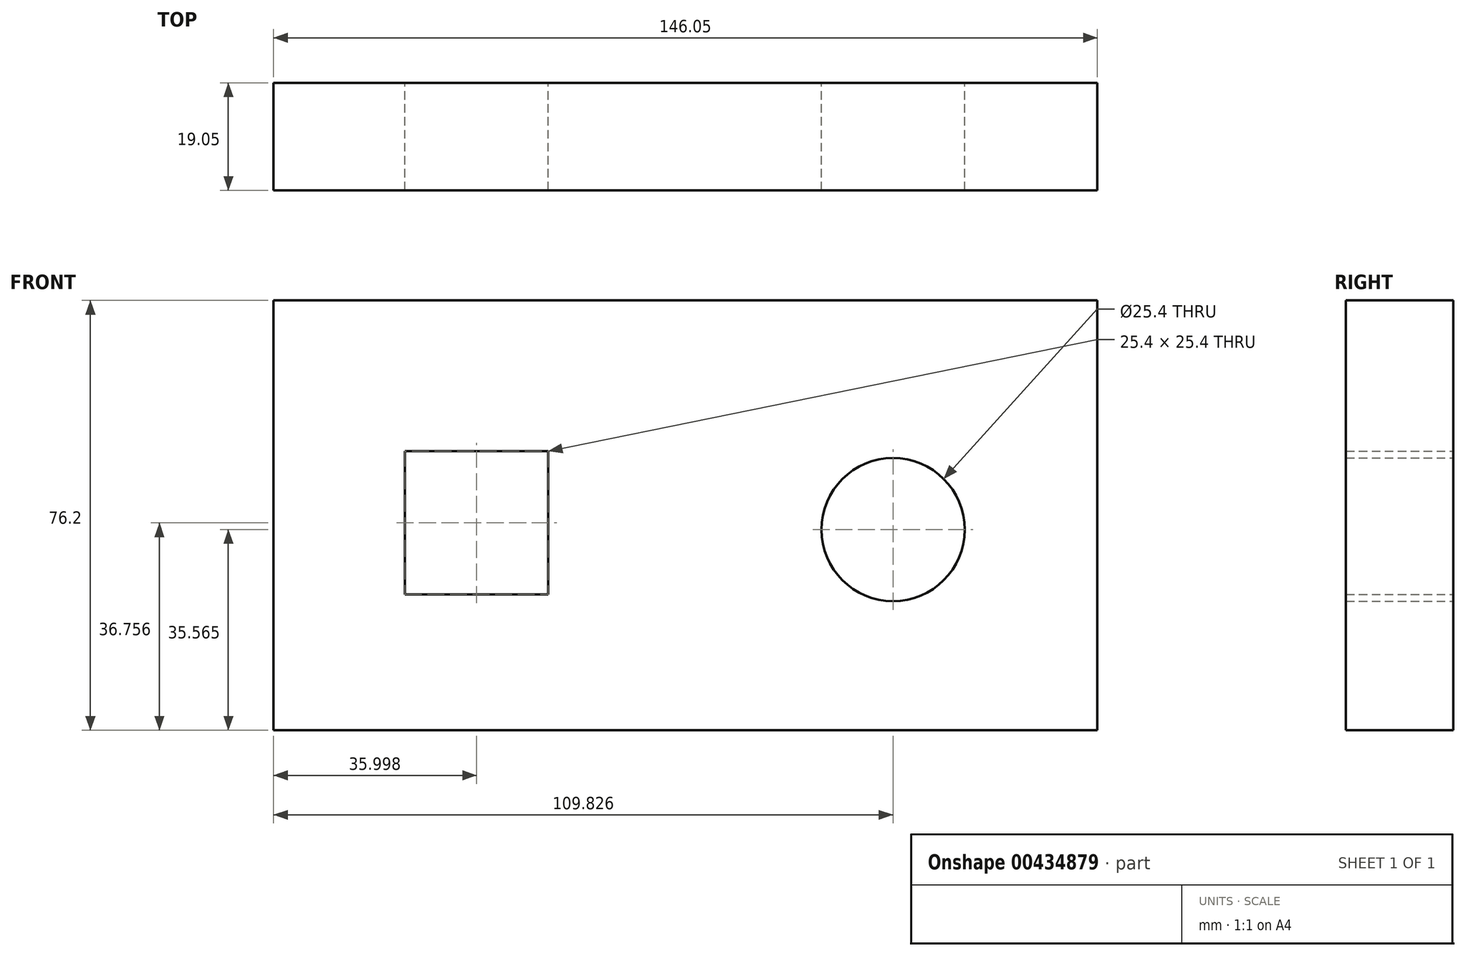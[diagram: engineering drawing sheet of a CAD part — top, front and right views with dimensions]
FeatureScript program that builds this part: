
annotation { "Feature Type Name" : "Feature", "Feature Type Description" : "" }
export const myFeature = defineFeature(function(context is Context, id is Id, definition is map)
    precondition{}
    {
        {
            var Q0;
            Q0=qCreatedBy(makeId("Front.planeOp"),FACE);
            var sketch = newSketch(context, id + "F0", { "sketchPlane" : qUnion([Q0])});
            skLineSegment(sketch, "E0.bottom", {"start": v(-73.14, -32.84) * mm, "end": v(72.91, -32.84) * mm});
            skLineSegment(sketch, "E0.top", {"start": v(-73.14, 43.36) * mm, "end": v(72.91, 43.36) * mm});
            skLineSegment(sketch, "E0.left", {"start": v(-73.14, -32.84) * mm, "end": v(-73.14, 43.36) * mm});
            skLineSegment(sketch, "E0.right", {"start": v(72.91, -32.84) * mm, "end": v(72.91, 43.36) * mm});
            skLineSegment(sketch, "E1.bottom", {"start": v(-49.84, 16.62) * mm, "end": v(-24.44, 16.62) * mm});
            skLineSegment(sketch, "E1.top", {"start": v(-49.84, -8.78) * mm, "end": v(-24.44, -8.78) * mm});
            skLineSegment(sketch, "E1.left", {"start": v(-49.84, 16.62) * mm, "end": v(-49.84, -8.78) * mm});
            skLineSegment(sketch, "E1.right", {"start": v(-24.44, 16.62) * mm, "end": v(-24.44, -8.78) * mm});
            skCircle(sketch, "E2", {"center": v(36.69, 2.72) * mm, "radius": 12.7 * mm});
            skSolve(sketch);
        }
        {
            var Q0;
            Q0=makeQuery(id+"F0.imprint","IMPRINT",FACE,{"disambiguationData":[TD([[makeQuery(id+"F0.imprint","IMPRINT",EDGE,{"derivedFrom":sQuery(id+"F0.wireOp",EDGE,"E0.bottom")}),1.0]])]});
            extrude(context, id + "F1", {"entities" : qUnion([Q0]), "depth" : 19.05 * mm});
        }
    });
